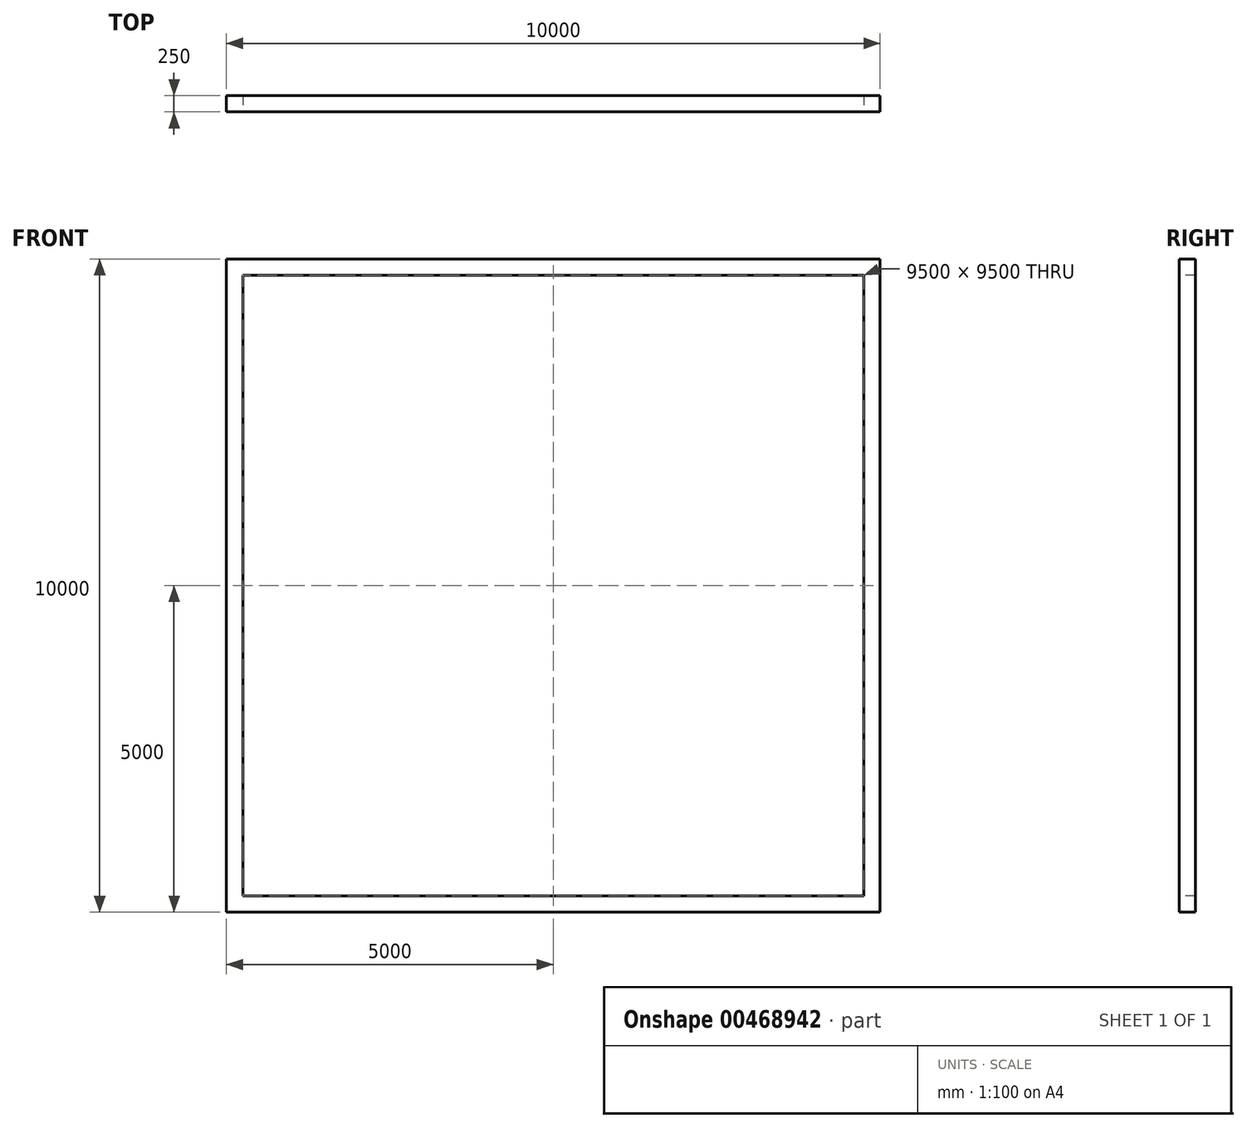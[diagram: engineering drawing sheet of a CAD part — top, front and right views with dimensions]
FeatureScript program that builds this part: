
annotation { "Feature Type Name" : "Feature", "Feature Type Description" : "" }
export const myFeature = defineFeature(function(context is Context, id is Id, definition is map)
    precondition{}
    {
        {
            var Q0;
            Q0=qCreatedBy(makeId("Front.planeOp"),FACE);
            var sketch = newSketch(context, id + "F0", { "sketchPlane" : qUnion([Q0])});
            skLineSegment(sketch, "E0.bottom", {"start": v(-5000, 5000) * mm, "end": v(5000, 5000) * mm});
            skLineSegment(sketch, "E0.top", {"start": v(-5000, -5000) * mm, "end": v(5000, -5000) * mm});
            skLineSegment(sketch, "E0.left", {"start": v(-5000, 5000) * mm, "end": v(-5000, -5000) * mm});
            skLineSegment(sketch, "E0.right", {"start": v(5000, 5000) * mm, "end": v(5000, -5000) * mm});
            skSolve(sketch);
        }
        {
            var Q0;
            Q0 = qSketchRegion(id + "F0", true);
            extrude(context, id + "F1", {"entities" : qUnion([Q0]), "endBound" : BoundingType.SYMMETRIC, "depth" : 250 * mm});
        }
        {
            var Q0;
            Q0=makeQuery(id+"F1.opExtrude","CAP_FACE",FACE,{"disambiguationData":[OSD([sQuery(id+"F0.wireOp",EDGE,"E0.bottom"),sQuery(id+"F0.wireOp",EDGE,"E0.top"),sQuery(id+"F0.wireOp",EDGE,"E0.left"),sQuery(id+"F0.wireOp",EDGE,"E0.right")])],"isStart":false});
            var sketch = newSketch(context, id + "F2", { "sketchPlane" : qUnion([Q0])});
            skLineSegment(sketch, "E1.bottom", {"start": v(-4750, 4750) * mm, "end": v(4750, 4750) * mm});
            skLineSegment(sketch, "E1.top", {"start": v(-4750, -4750) * mm, "end": v(4750, -4750) * mm});
            skLineSegment(sketch, "E1.left", {"start": v(-4750, 4750) * mm, "end": v(-4750, -4750) * mm});
            skLineSegment(sketch, "E1.right", {"start": v(4750, 4750) * mm, "end": v(4750, -4750) * mm});
            skSolve(sketch);
        }
        {
            var Q0;
            Q0 = qSketchRegion(id + "F2", true);
            var Q1;
            Q1=makeQuery(id+"F1.opExtrude","CAP_FACE",FACE,{"disambiguationData":[OSD([sQuery(id+"F0.wireOp",EDGE,"E0.bottom"),sQuery(id+"F0.wireOp",EDGE,"E0.top"),sQuery(id+"F0.wireOp",EDGE,"E0.left"),sQuery(id+"F0.wireOp",EDGE,"E0.right")])],"isStart":true});
            extrude(context, id + "F3", {"entities" : qUnion([Q0]), "operationType" : NewBodyOperationType.REMOVE, "endBound" : BoundingType.UP_TO_SURFACE, "oppositeDirection" : true, "endBoundEntityFace" : qUnion([Q1]), "depth" : 25 * mm});
        }
    });
